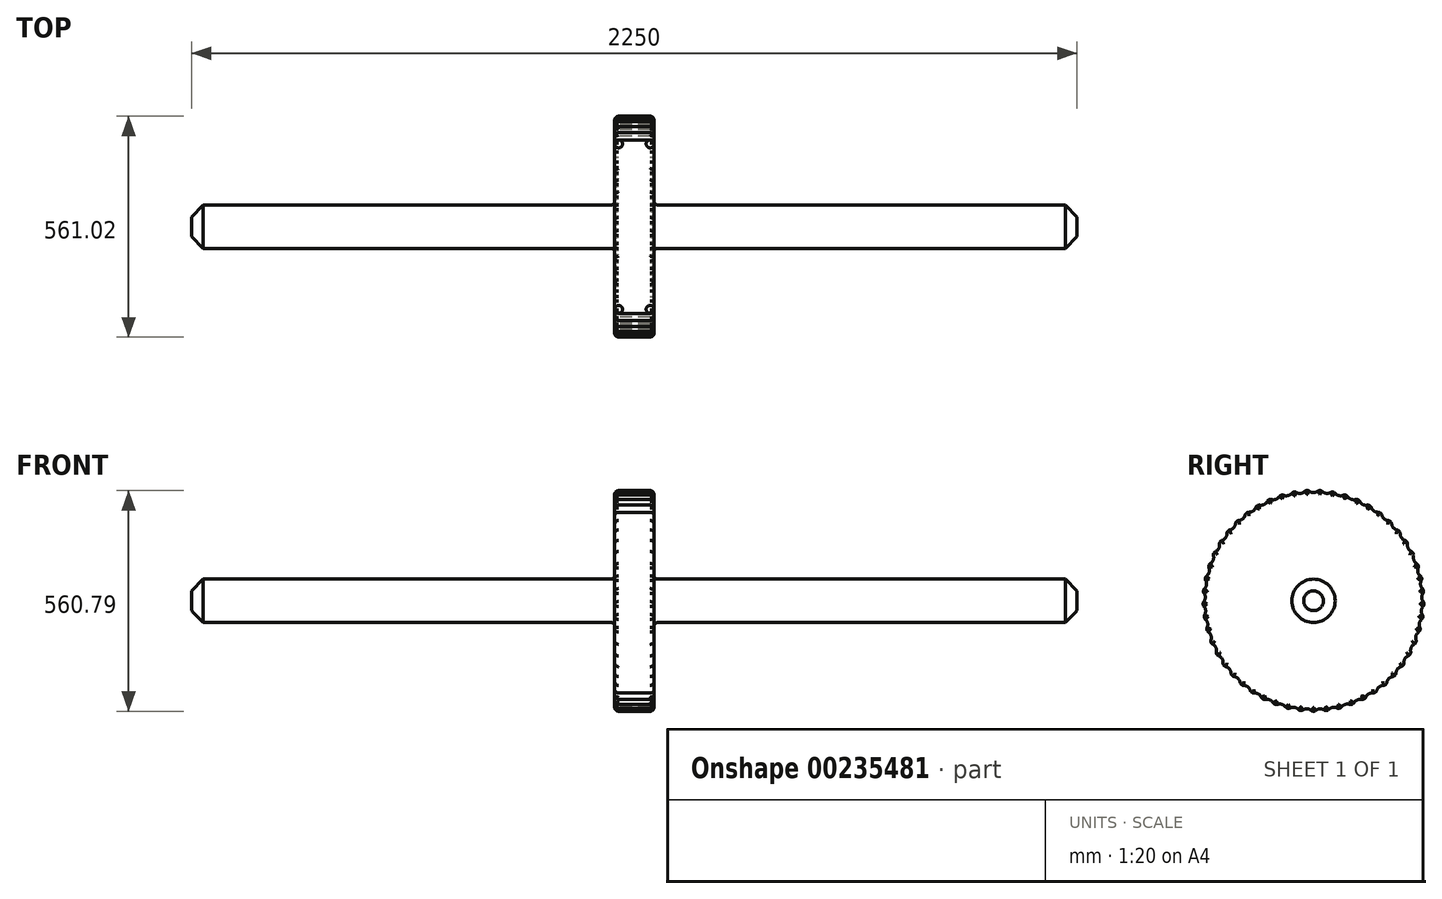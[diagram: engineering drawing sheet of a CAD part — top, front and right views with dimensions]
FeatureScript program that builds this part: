
annotation { "Feature Type Name" : "Feature", "Feature Type Description" : "" }
export const myFeature = defineFeature(function(context is Context, id is Id, definition is map)
    precondition{}
    {
        {
            var Q0;
            Q0=qCreatedBy(makeId("Right.planeOp"),FACE);
            var sketch = newSketch(context, id + "F0", { "sketchPlane" : qUnion([Q0])});
            skCircle(sketch, "E0", {"center": v(0, 0) * mm, "radius": 55 * mm});
            skSolve(sketch);
        }
        {
            var Q0;
            Q0 = qSketchRegion(id + "F0", true);
            extrude(context, id + "F1", {"entities" : qUnion([Q0]), "endBound" : BoundingType.SYMMETRIC, "depth" : 2250 * mm});
        }
        {
            var Q0;
            Q0=makeQuery(id+"F1.opExtrude","CAP_EDGE",EDGE,{"disambiguationData":[OSD([sQuery(id+"F0.wireOp",EDGE,"E0")])],"isStart":false});
            var Q1;
            Q1=makeQuery(id+"F1.opExtrude","CAP_EDGE",EDGE,{"disambiguationData":[OSD([sQuery(id+"F0.wireOp",EDGE,"E0")])],"isStart":true});
            chamfer(context, id + "F2", {"entities" : qUnion([Q0, Q1]), "width" : 30 * mm, "tangentPropagation" : true});
        }
        {
            var Q0;
            Q0=qCreatedBy(makeId("Right.planeOp"),FACE);
            var sketch = newSketch(context, id + "F3", { "sketchPlane" : qUnion([Q0])});
            skCircle(sketch, "E1", {"center": v(0, 0) * mm, "radius": 275 * mm, "construction": true});
            skCircle(sketch, "E2", {"center": v(0, 0) * mm, "radius": 310 * mm, "construction": true});
            skArc(sketch, "E3", {"start": v(-17.5, 291.98) * mm, "mid": v(0, 275) * mm, "end": v(17.5, 291.98) * mm});
            skCircle(sketch, "E4", {"center": v(0, 0) * mm, "radius": 292.5 * mm, "construction": true});
            skArc(sketch, "E5.1.0", {"start": v(-51.9, 287.86) * mm, "mid": v(-32.53, 273.07) * mm, "end": v(-17.16, 292) * mm});
            skArc(sketch, "E5.2.0", {"start": v(-85.58, 279.7) * mm, "mid": v(-64.6, 267.3) * mm, "end": v(-51.58, 287.92) * mm});
            skArc(sketch, "E5.3.0", {"start": v(-118.06, 267.61) * mm, "mid": v(-95.76, 257.8) * mm, "end": v(-85.27, 279.8) * mm});
            skArc(sketch, "E5.4.0", {"start": v(-148.89, 251.77) * mm, "mid": v(-125.57, 244.66) * mm, "end": v(-117.76, 267.75) * mm});
            skArc(sketch, "E5.5.0", {"start": v(-177.62, 232.4) * mm, "mid": v(-153.63, 228.09) * mm, "end": v(-148.6, 251.94) * mm});
            skArc(sketch, "E5.6.0", {"start": v(-203.86, 209.76) * mm, "mid": v(-179.53, 208.32) * mm, "end": v(-177.36, 232.6) * mm});
            skArc(sketch, "E5.7.0", {"start": v(-227.24, 184.17) * mm, "mid": v(-202.9, 185.62) * mm, "end": v(-203.62, 209.99) * mm});
            skArc(sketch, "E5.8.0", {"start": v(-247.42, 156) * mm, "mid": v(-223.43, 160.32) * mm, "end": v(-227.03, 184.43) * mm});
            skArc(sketch, "E5.9.0", {"start": v(-264.14, 125.65) * mm, "mid": v(-240.83, 132.77) * mm, "end": v(-247.25, 156.28) * mm});
            skArc(sketch, "E5.10.0", {"start": v(-277.15, 93.52) * mm, "mid": v(-254.84, 103.35) * mm, "end": v(-264, 125.94) * mm});
            skArc(sketch, "E5.11.0", {"start": v(-286.26, 60.09) * mm, "mid": v(-265.27, 72.49) * mm, "end": v(-277.04, 93.83) * mm});
            skArc(sketch, "E5.12.0", {"start": v(-291.36, 25.8) * mm, "mid": v(-271.99, 40.6) * mm, "end": v(-286.2, 60.4) * mm});
            skArc(sketch, "E5.13.0", {"start": v(-292.37, -8.83) * mm, "mid": v(-274.88, 8.15) * mm, "end": v(-291.33, 26.14) * mm});
            skArc(sketch, "E5.14.0", {"start": v(-289.27, -43.35) * mm, "mid": v(-273.91, -24.42) * mm, "end": v(-292.38, -8.5) * mm});
            skArc(sketch, "E5.15.0", {"start": v(-282.11, -77.26) * mm, "mid": v(-269.1, -56.64) * mm, "end": v(-289.32, -43.02) * mm});
            skArc(sketch, "E5.16.0", {"start": v(-271, -110.08) * mm, "mid": v(-260.51, -88.07) * mm, "end": v(-282.2, -76.94) * mm});
            skArc(sketch, "E5.17.0", {"start": v(-256.07, -141.36) * mm, "mid": v(-248.27, -118.27) * mm, "end": v(-271.12, -109.78) * mm});
            skArc(sketch, "E5.18.0", {"start": v(-237.56, -170.66) * mm, "mid": v(-232.54, -146.8) * mm, "end": v(-256.23, -141.07) * mm});
            skArc(sketch, "E5.19.0", {"start": v(-215.7, -197.55) * mm, "mid": v(-213.54, -173.27) * mm, "end": v(-237.75, -170.39) * mm});
            skArc(sketch, "E5.20.0", {"start": v(-190.83, -221.68) * mm, "mid": v(-191.55, -197.31) * mm, "end": v(-215.93, -197.31) * mm});
            skArc(sketch, "E5.21.0", {"start": v(-163.27, -242.7) * mm, "mid": v(-166.87, -218.58) * mm, "end": v(-191.08, -221.46) * mm});
            skArc(sketch, "E5.22.0", {"start": v(-133.42, -260.3) * mm, "mid": v(-139.85, -236.79) * mm, "end": v(-163.54, -242.5) * mm});
            skArc(sketch, "E5.23.0", {"start": v(-101.7, -274.25) * mm, "mid": v(-110.86, -251.67) * mm, "end": v(-133.71, -260.15) * mm});
            skArc(sketch, "E5.24.0", {"start": v(-68.54, -284.36) * mm, "mid": v(-80.32, -263.01) * mm, "end": v(-102, -274.14) * mm});
            skArc(sketch, "E5.25.0", {"start": v(-34.43, -290.47) * mm, "mid": v(-48.64, -270.66) * mm, "end": v(-68.86, -284.28) * mm});
            skArc(sketch, "E5.26.0", {"start": v(0.16, -292.5) * mm, "mid": v(-16.3, -274.52) * mm, "end": v(-34.76, -290.43) * mm});
            skArc(sketch, "E5.27.0", {"start": v(34.76, -290.43) * mm, "mid": v(16.3, -274.52) * mm, "end": v(-0.16, -292.5) * mm});
            skArc(sketch, "E5.28.0", {"start": v(68.86, -284.28) * mm, "mid": v(48.64, -270.66) * mm, "end": v(34.43, -290.47) * mm});
            skArc(sketch, "E5.29.0", {"start": v(102, -274.14) * mm, "mid": v(80.32, -263.01) * mm, "end": v(68.54, -284.36) * mm});
            skArc(sketch, "E5.30.0", {"start": v(133.71, -260.15) * mm, "mid": v(110.86, -251.67) * mm, "end": v(101.7, -274.25) * mm});
            skArc(sketch, "E5.31.0", {"start": v(163.54, -242.5) * mm, "mid": v(139.85, -236.79) * mm, "end": v(133.42, -260.3) * mm});
            skArc(sketch, "E5.32.0", {"start": v(191.08, -221.46) * mm, "mid": v(166.87, -218.58) * mm, "end": v(163.27, -242.7) * mm});
            skArc(sketch, "E5.33.0", {"start": v(215.93, -197.31) * mm, "mid": v(191.55, -197.31) * mm, "end": v(190.83, -221.68) * mm});
            skArc(sketch, "E5.34.0", {"start": v(237.75, -170.39) * mm, "mid": v(213.54, -173.27) * mm, "end": v(215.7, -197.55) * mm});
            skArc(sketch, "E5.35.0", {"start": v(256.23, -141.07) * mm, "mid": v(232.54, -146.8) * mm, "end": v(237.56, -170.66) * mm});
            skArc(sketch, "E5.36.0", {"start": v(271.12, -109.78) * mm, "mid": v(248.27, -118.27) * mm, "end": v(256.07, -141.36) * mm});
            skArc(sketch, "E5.37.0", {"start": v(282.2, -76.94) * mm, "mid": v(260.51, -88.07) * mm, "end": v(271, -110.08) * mm});
            skArc(sketch, "E5.38.0", {"start": v(289.32, -43.02) * mm, "mid": v(269.1, -56.64) * mm, "end": v(282.11, -77.26) * mm});
            skArc(sketch, "E5.39.0", {"start": v(292.38, -8.5) * mm, "mid": v(273.91, -24.42) * mm, "end": v(289.27, -43.35) * mm});
            skArc(sketch, "E5.40.0", {"start": v(291.33, 26.14) * mm, "mid": v(274.88, 8.15) * mm, "end": v(292.37, -8.83) * mm});
            skArc(sketch, "E5.41.0", {"start": v(286.2, 60.4) * mm, "mid": v(271.99, 40.6) * mm, "end": v(291.36, 25.8) * mm});
            skArc(sketch, "E5.42.0", {"start": v(277.04, 93.83) * mm, "mid": v(265.27, 72.49) * mm, "end": v(286.26, 60.09) * mm});
            skArc(sketch, "E5.43.0", {"start": v(264, 125.94) * mm, "mid": v(254.84, 103.35) * mm, "end": v(277.15, 93.52) * mm});
            skArc(sketch, "E5.44.0", {"start": v(247.25, 156.28) * mm, "mid": v(240.83, 132.77) * mm, "end": v(264.14, 125.65) * mm});
            skArc(sketch, "E5.45.0", {"start": v(227.03, 184.43) * mm, "mid": v(223.43, 160.32) * mm, "end": v(247.42, 156) * mm});
            skArc(sketch, "E5.46.0", {"start": v(203.62, 209.99) * mm, "mid": v(202.9, 185.62) * mm, "end": v(227.24, 184.17) * mm});
            skArc(sketch, "E5.47.0", {"start": v(177.36, 232.6) * mm, "mid": v(179.53, 208.32) * mm, "end": v(203.86, 209.76) * mm});
            skArc(sketch, "E5.48.0", {"start": v(148.6, 251.94) * mm, "mid": v(153.63, 228.09) * mm, "end": v(177.62, 232.4) * mm});
            skArc(sketch, "E5.49.0", {"start": v(117.76, 267.75) * mm, "mid": v(125.57, 244.66) * mm, "end": v(148.89, 251.77) * mm});
            skArc(sketch, "E6.2.50.0", {"start": v(85.27, 279.8) * mm, "mid": v(95.76, 257.8) * mm, "end": v(118.06, 267.61) * mm});
            skArc(sketch, "E6.2.51.0", {"start": v(51.58, 287.92) * mm, "mid": v(64.6, 267.3) * mm, "end": v(85.58, 279.7) * mm});
            skArc(sketch, "E7.2.52.0", {"start": v(17.16, 292) * mm, "mid": v(32.53, 273.07) * mm, "end": v(51.9, 287.86) * mm});
            skSolve(sketch);
        }
        {
            var Q0;
            Q0=makeQuery(id+"F3.imprint","IMPRINT",FACE,{"disambiguationData":[TD([[makeQuery(id+"F3.imprint","IMPRINT",EDGE,{"derivedFrom":sQuery(id+"F3.wireOp",EDGE,"E1")}),1.0]])]});
            var Q1;
            {var subQ48=sQuery(id+"F3.wireOp",EDGE,"E5.1.0");var subQ49=sQuery(id+"F3.wireOp",EDGE,"E3");var subQ50=makeQuery(id+"F3.imprint","INTERSECT",VERTEX,{"derivedFrom":[subQ49,subQ48]});Q1=makeQuery(id+"F3.imprint","IMPRINT",FACE,{"disambiguationData":[TD([[makeQuery(id+"F3.imprint","IMPRINT",EDGE,{"disambiguationData":[TD([[subQ50,-1.0]])],"derivedFrom":subQ49}),-1.0]])]});}
            extrude(context, id + "F4", {"entities" : qUnion([Q0, Q1]), "operationType" : NewBodyOperationType.ADD, "endBound" : BoundingType.SYMMETRIC, "depth" : 100 * mm});
        }
        {
            var Q0;
            Q0=makeQuery(id+"F4.opExtrude","CAP_FACE",FACE,{"disambiguationData":[OSD([sQuery(id+"F3.wireOp",EDGE,"E3"),sQuery(id+"F3.wireOp",EDGE,"E5.1.0"),sQuery(id+"F3.wireOp",EDGE,"E5.2.0"),sQuery(id+"F3.wireOp",EDGE,"E5.3.0"),sQuery(id+"F3.wireOp",EDGE,"E5.4.0"),sQuery(id+"F3.wireOp",EDGE,"E5.5.0"),sQuery(id+"F3.wireOp",EDGE,"E5.6.0"),sQuery(id+"F3.wireOp",EDGE,"E5.7.0"),sQuery(id+"F3.wireOp",EDGE,"E5.8.0"),sQuery(id+"F3.wireOp",EDGE,"E5.9.0"),sQuery(id+"F3.wireOp",EDGE,"E5.10.0"),sQuery(id+"F3.wireOp",EDGE,"E5.11.0"),sQuery(id+"F3.wireOp",EDGE,"E5.12.0"),sQuery(id+"F3.wireOp",EDGE,"E5.13.0"),sQuery(id+"F3.wireOp",EDGE,"E5.14.0"),sQuery(id+"F3.wireOp",EDGE,"E5.15.0"),sQuery(id+"F3.wireOp",EDGE,"E5.16.0"),sQuery(id+"F3.wireOp",EDGE,"E5.17.0"),sQuery(id+"F3.wireOp",EDGE,"E5.18.0"),sQuery(id+"F3.wireOp",EDGE,"E5.19.0"),sQuery(id+"F3.wireOp",EDGE,"E5.20.0"),sQuery(id+"F3.wireOp",EDGE,"E5.21.0"),sQuery(id+"F3.wireOp",EDGE,"E5.22.0"),sQuery(id+"F3.wireOp",EDGE,"E5.23.0"),sQuery(id+"F3.wireOp",EDGE,"E5.24.0"),sQuery(id+"F3.wireOp",EDGE,"E5.25.0"),sQuery(id+"F3.wireOp",EDGE,"E5.26.0"),sQuery(id+"F3.wireOp",EDGE,"E5.27.0"),sQuery(id+"F3.wireOp",EDGE,"E5.28.0"),sQuery(id+"F3.wireOp",EDGE,"E5.29.0"),sQuery(id+"F3.wireOp",EDGE,"E5.30.0"),sQuery(id+"F3.wireOp",EDGE,"E5.31.0"),sQuery(id+"F3.wireOp",EDGE,"E5.32.0"),sQuery(id+"F3.wireOp",EDGE,"E5.33.0"),sQuery(id+"F3.wireOp",EDGE,"E5.34.0"),sQuery(id+"F3.wireOp",EDGE,"E5.35.0"),sQuery(id+"F3.wireOp",EDGE,"E5.36.0"),sQuery(id+"F3.wireOp",EDGE,"E5.37.0"),sQuery(id+"F3.wireOp",EDGE,"E5.38.0"),sQuery(id+"F3.wireOp",EDGE,"E5.39.0"),sQuery(id+"F3.wireOp",EDGE,"E5.40.0"),sQuery(id+"F3.wireOp",EDGE,"E5.41.0"),sQuery(id+"F3.wireOp",EDGE,"E5.42.0"),sQuery(id+"F3.wireOp",EDGE,"E5.43.0"),sQuery(id+"F3.wireOp",EDGE,"E5.44.0"),sQuery(id+"F3.wireOp",EDGE,"E5.45.0"),sQuery(id+"F3.wireOp",EDGE,"E5.46.0"),sQuery(id+"F3.wireOp",EDGE,"E5.47.0"),sQuery(id+"F3.wireOp",EDGE,"E5.48.0"),sQuery(id+"F3.wireOp",EDGE,"E5.49.0"),sQuery(id+"F3.wireOp",EDGE,"E6.2.50.0"),sQuery(id+"F3.wireOp",EDGE,"E6.2.51.0"),sQuery(id+"F3.wireOp",EDGE,"E7.2.52.0")])],"isStart":false});
            var Q1;
            Q1=makeQuery(id+"F4.opExtrude","CAP_FACE",FACE,{"disambiguationData":[OSD([sQuery(id+"F3.wireOp",EDGE,"E3"),sQuery(id+"F3.wireOp",EDGE,"E5.1.0"),sQuery(id+"F3.wireOp",EDGE,"E5.2.0"),sQuery(id+"F3.wireOp",EDGE,"E5.3.0"),sQuery(id+"F3.wireOp",EDGE,"E5.4.0"),sQuery(id+"F3.wireOp",EDGE,"E5.5.0"),sQuery(id+"F3.wireOp",EDGE,"E5.6.0"),sQuery(id+"F3.wireOp",EDGE,"E5.7.0"),sQuery(id+"F3.wireOp",EDGE,"E5.8.0"),sQuery(id+"F3.wireOp",EDGE,"E5.9.0"),sQuery(id+"F3.wireOp",EDGE,"E5.10.0"),sQuery(id+"F3.wireOp",EDGE,"E5.11.0"),sQuery(id+"F3.wireOp",EDGE,"E5.12.0"),sQuery(id+"F3.wireOp",EDGE,"E5.13.0"),sQuery(id+"F3.wireOp",EDGE,"E5.14.0"),sQuery(id+"F3.wireOp",EDGE,"E5.15.0"),sQuery(id+"F3.wireOp",EDGE,"E5.16.0"),sQuery(id+"F3.wireOp",EDGE,"E5.17.0"),sQuery(id+"F3.wireOp",EDGE,"E5.18.0"),sQuery(id+"F3.wireOp",EDGE,"E5.19.0"),sQuery(id+"F3.wireOp",EDGE,"E5.20.0"),sQuery(id+"F3.wireOp",EDGE,"E5.21.0"),sQuery(id+"F3.wireOp",EDGE,"E5.22.0"),sQuery(id+"F3.wireOp",EDGE,"E5.23.0"),sQuery(id+"F3.wireOp",EDGE,"E5.24.0"),sQuery(id+"F3.wireOp",EDGE,"E5.25.0"),sQuery(id+"F3.wireOp",EDGE,"E5.26.0"),sQuery(id+"F3.wireOp",EDGE,"E5.27.0"),sQuery(id+"F3.wireOp",EDGE,"E5.28.0"),sQuery(id+"F3.wireOp",EDGE,"E5.29.0"),sQuery(id+"F3.wireOp",EDGE,"E5.30.0"),sQuery(id+"F3.wireOp",EDGE,"E5.31.0"),sQuery(id+"F3.wireOp",EDGE,"E5.32.0"),sQuery(id+"F3.wireOp",EDGE,"E5.33.0"),sQuery(id+"F3.wireOp",EDGE,"E5.34.0"),sQuery(id+"F3.wireOp",EDGE,"E5.35.0"),sQuery(id+"F3.wireOp",EDGE,"E5.36.0"),sQuery(id+"F3.wireOp",EDGE,"E5.37.0"),sQuery(id+"F3.wireOp",EDGE,"E5.38.0"),sQuery(id+"F3.wireOp",EDGE,"E5.39.0"),sQuery(id+"F3.wireOp",EDGE,"E5.40.0"),sQuery(id+"F3.wireOp",EDGE,"E5.41.0"),sQuery(id+"F3.wireOp",EDGE,"E5.42.0"),sQuery(id+"F3.wireOp",EDGE,"E5.43.0"),sQuery(id+"F3.wireOp",EDGE,"E5.44.0"),sQuery(id+"F3.wireOp",EDGE,"E5.45.0"),sQuery(id+"F3.wireOp",EDGE,"E5.46.0"),sQuery(id+"F3.wireOp",EDGE,"E5.47.0"),sQuery(id+"F3.wireOp",EDGE,"E5.48.0"),sQuery(id+"F3.wireOp",EDGE,"E5.49.0"),sQuery(id+"F3.wireOp",EDGE,"E6.2.50.0"),sQuery(id+"F3.wireOp",EDGE,"E6.2.51.0"),sQuery(id+"F3.wireOp",EDGE,"E7.2.52.0")])],"isStart":true});
            fillet(context, id + "F5", {"entities" : qUnion([Q0, Q1]), "radius" : 10 * mm, "tangentPropagation" : true, "allowEdgeOverflow" : false});
        }
        {
            var Q0;
            Q0=makeQuery(id+"F4.opExtrude","SWEPT_EDGE",EDGE,{"disambiguationData":[OSD([sQuery(id+"F3.wireOp",EDGE,"E5.22.0"),sQuery(id+"F3.wireOp",EDGE,"E5.23.0")])]});
            var Q1;
            Q1=makeQuery(id+"F4.opExtrude","SWEPT_EDGE",EDGE,{"disambiguationData":[OSD([sQuery(id+"F3.wireOp",EDGE,"E5.21.0"),sQuery(id+"F3.wireOp",EDGE,"E5.22.0")])]});
            var Q2;
            Q2=makeQuery(id+"F4.opExtrude","SWEPT_EDGE",EDGE,{"disambiguationData":[OSD([sQuery(id+"F3.wireOp",EDGE,"E5.20.0"),sQuery(id+"F3.wireOp",EDGE,"E5.21.0")])]});
            var Q3;
            Q3=makeQuery(id+"F4.opExtrude","SWEPT_EDGE",EDGE,{"disambiguationData":[OSD([sQuery(id+"F3.wireOp",EDGE,"E5.18.0"),sQuery(id+"F3.wireOp",EDGE,"E5.19.0")])]});
            var Q4;
            Q4=makeQuery(id+"F4.opExtrude","SWEPT_EDGE",EDGE,{"disambiguationData":[OSD([sQuery(id+"F3.wireOp",EDGE,"E5.17.0"),sQuery(id+"F3.wireOp",EDGE,"E5.18.0")])]});
            var Q5;
            Q5=makeQuery(id+"F4.opExtrude","SWEPT_EDGE",EDGE,{"disambiguationData":[OSD([sQuery(id+"F3.wireOp",EDGE,"E5.19.0"),sQuery(id+"F3.wireOp",EDGE,"E5.20.0")])]});
            var Q6;
            Q6=makeQuery(id+"F4.opExtrude","SWEPT_EDGE",EDGE,{"disambiguationData":[OSD([sQuery(id+"F3.wireOp",EDGE,"E5.16.0"),sQuery(id+"F3.wireOp",EDGE,"E5.17.0")])]});
            var Q7;
            Q7=makeQuery(id+"F4.opExtrude","SWEPT_EDGE",EDGE,{"disambiguationData":[OSD([sQuery(id+"F3.wireOp",EDGE,"E5.15.0"),sQuery(id+"F3.wireOp",EDGE,"E5.16.0")])]});
            var Q8;
            Q8=makeQuery(id+"F4.opExtrude","SWEPT_EDGE",EDGE,{"disambiguationData":[OSD([sQuery(id+"F3.wireOp",EDGE,"E5.14.0"),sQuery(id+"F3.wireOp",EDGE,"E5.15.0")])]});
            var Q9;
            Q9=makeQuery(id+"F4.opExtrude","SWEPT_EDGE",EDGE,{"disambiguationData":[OSD([sQuery(id+"F3.wireOp",EDGE,"E5.13.0"),sQuery(id+"F3.wireOp",EDGE,"E5.14.0")])]});
            var Q10;
            Q10=makeQuery(id+"F4.opExtrude","SWEPT_EDGE",EDGE,{"disambiguationData":[OSD([sQuery(id+"F3.wireOp",EDGE,"E5.12.0"),sQuery(id+"F3.wireOp",EDGE,"E5.13.0")])]});
            var Q11;
            Q11=makeQuery(id+"F4.opExtrude","SWEPT_EDGE",EDGE,{"disambiguationData":[OSD([sQuery(id+"F3.wireOp",EDGE,"E5.11.0"),sQuery(id+"F3.wireOp",EDGE,"E5.12.0")])]});
            var Q12;
            Q12=makeQuery(id+"F4.opExtrude","SWEPT_EDGE",EDGE,{"disambiguationData":[OSD([sQuery(id+"F3.wireOp",EDGE,"E5.10.0"),sQuery(id+"F3.wireOp",EDGE,"E5.11.0")])]});
            var Q13;
            Q13=makeQuery(id+"F4.opExtrude","SWEPT_EDGE",EDGE,{"disambiguationData":[OSD([sQuery(id+"F3.wireOp",EDGE,"E5.9.0"),sQuery(id+"F3.wireOp",EDGE,"E5.10.0")])]});
            var Q14;
            Q14=makeQuery(id+"F4.opExtrude","SWEPT_EDGE",EDGE,{"disambiguationData":[OSD([sQuery(id+"F3.wireOp",EDGE,"E5.8.0"),sQuery(id+"F3.wireOp",EDGE,"E5.9.0")])]});
            var Q15;
            Q15=makeQuery(id+"F4.opExtrude","SWEPT_EDGE",EDGE,{"disambiguationData":[OSD([sQuery(id+"F3.wireOp",EDGE,"E5.7.0"),sQuery(id+"F3.wireOp",EDGE,"E5.8.0")])]});
            var Q16;
            Q16=makeQuery(id+"F4.opExtrude","SWEPT_EDGE",EDGE,{"disambiguationData":[OSD([sQuery(id+"F3.wireOp",EDGE,"E5.8.0"),sQuery(id+"F3.wireOp",EDGE,"E5.9.0")])]});
            var Q17;
            Q17=makeQuery(id+"F4.opExtrude","SWEPT_EDGE",EDGE,{"disambiguationData":[OSD([sQuery(id+"F3.wireOp",EDGE,"E5.6.0"),sQuery(id+"F3.wireOp",EDGE,"E5.7.0")])]});
            var Q18;
            Q18=makeQuery(id+"F4.opExtrude","SWEPT_EDGE",EDGE,{"disambiguationData":[OSD([sQuery(id+"F3.wireOp",EDGE,"E5.5.0"),sQuery(id+"F3.wireOp",EDGE,"E5.6.0")])]});
            var Q19;
            Q19=makeQuery(id+"F4.opExtrude","SWEPT_EDGE",EDGE,{"disambiguationData":[OSD([sQuery(id+"F3.wireOp",EDGE,"E5.4.0"),sQuery(id+"F3.wireOp",EDGE,"E5.5.0")])]});
            var Q20;
            Q20=makeQuery(id+"F4.opExtrude","SWEPT_EDGE",EDGE,{"disambiguationData":[OSD([sQuery(id+"F3.wireOp",EDGE,"E5.3.0"),sQuery(id+"F3.wireOp",EDGE,"E5.4.0")])]});
            var Q21;
            Q21=makeQuery(id+"F4.opExtrude","SWEPT_EDGE",EDGE,{"disambiguationData":[OSD([sQuery(id+"F3.wireOp",EDGE,"E5.2.0"),sQuery(id+"F3.wireOp",EDGE,"E5.3.0")])]});
            var Q22;
            Q22=makeQuery(id+"F4.opExtrude","SWEPT_EDGE",EDGE,{"disambiguationData":[OSD([sQuery(id+"F3.wireOp",EDGE,"E5.1.0"),sQuery(id+"F3.wireOp",EDGE,"E5.2.0")])]});
            var Q23;
            Q23=makeQuery(id+"F4.opExtrude","SWEPT_EDGE",EDGE,{"disambiguationData":[OSD([sQuery(id+"F3.wireOp",EDGE,"E3"),sQuery(id+"F3.wireOp",EDGE,"E5.1.0")])]});
            var Q24;
            Q24=makeQuery(id+"F4.opExtrude","SWEPT_EDGE",EDGE,{"disambiguationData":[OSD([sQuery(id+"F3.wireOp",EDGE,"E3"),sQuery(id+"F3.wireOp",EDGE,"E7.2.52.0")])]});
            var Q25;
            Q25=makeQuery(id+"F4.opExtrude","SWEPT_EDGE",EDGE,{"disambiguationData":[OSD([sQuery(id+"F3.wireOp",EDGE,"E6.2.51.0"),sQuery(id+"F3.wireOp",EDGE,"E7.2.52.0")])]});
            var Q26;
            Q26=makeQuery(id+"F4.opExtrude","SWEPT_EDGE",EDGE,{"disambiguationData":[OSD([sQuery(id+"F3.wireOp",EDGE,"E6.2.50.0"),sQuery(id+"F3.wireOp",EDGE,"E6.2.51.0")])]});
            var Q27;
            Q27=makeQuery(id+"F4.opExtrude","SWEPT_EDGE",EDGE,{"disambiguationData":[OSD([sQuery(id+"F3.wireOp",EDGE,"E5.49.0"),sQuery(id+"F3.wireOp",EDGE,"E6.2.50.0")])]});
            var Q28;
            Q28=makeQuery(id+"F4.opExtrude","SWEPT_EDGE",EDGE,{"disambiguationData":[OSD([sQuery(id+"F3.wireOp",EDGE,"E5.48.0"),sQuery(id+"F3.wireOp",EDGE,"E5.49.0")])]});
            var Q29;
            Q29=makeQuery(id+"F4.opExtrude","SWEPT_EDGE",EDGE,{"disambiguationData":[OSD([sQuery(id+"F3.wireOp",EDGE,"E5.47.0"),sQuery(id+"F3.wireOp",EDGE,"E5.48.0")])]});
            var Q30;
            Q30=makeQuery(id+"F4.opExtrude","SWEPT_EDGE",EDGE,{"disambiguationData":[OSD([sQuery(id+"F3.wireOp",EDGE,"E5.46.0"),sQuery(id+"F3.wireOp",EDGE,"E5.47.0")])]});
            var Q31;
            Q31=makeQuery(id+"F4.opExtrude","SWEPT_EDGE",EDGE,{"disambiguationData":[OSD([sQuery(id+"F3.wireOp",EDGE,"E5.45.0"),sQuery(id+"F3.wireOp",EDGE,"E5.46.0")])]});
            var Q32;
            Q32=makeQuery(id+"F4.opExtrude","SWEPT_EDGE",EDGE,{"disambiguationData":[OSD([sQuery(id+"F3.wireOp",EDGE,"E5.44.0"),sQuery(id+"F3.wireOp",EDGE,"E5.45.0")])]});
            var Q33;
            Q33=makeQuery(id+"F4.opExtrude","SWEPT_EDGE",EDGE,{"disambiguationData":[OSD([sQuery(id+"F3.wireOp",EDGE,"E5.43.0"),sQuery(id+"F3.wireOp",EDGE,"E5.44.0")])]});
            var Q34;
            Q34=makeQuery(id+"F4.opExtrude","SWEPT_EDGE",EDGE,{"disambiguationData":[OSD([sQuery(id+"F3.wireOp",EDGE,"E5.42.0"),sQuery(id+"F3.wireOp",EDGE,"E5.43.0")])]});
            var Q35;
            Q35=makeQuery(id+"F4.opExtrude","SWEPT_EDGE",EDGE,{"disambiguationData":[OSD([sQuery(id+"F3.wireOp",EDGE,"E5.41.0"),sQuery(id+"F3.wireOp",EDGE,"E5.42.0")])]});
            var Q36;
            Q36=makeQuery(id+"F4.opExtrude","SWEPT_EDGE",EDGE,{"disambiguationData":[OSD([sQuery(id+"F3.wireOp",EDGE,"E5.40.0"),sQuery(id+"F3.wireOp",EDGE,"E5.41.0")])]});
            var Q37;
            Q37=makeQuery(id+"F4.opExtrude","SWEPT_EDGE",EDGE,{"disambiguationData":[OSD([sQuery(id+"F3.wireOp",EDGE,"E5.39.0"),sQuery(id+"F3.wireOp",EDGE,"E5.40.0")])]});
            var Q38;
            Q38=makeQuery(id+"F4.opExtrude","SWEPT_EDGE",EDGE,{"disambiguationData":[OSD([sQuery(id+"F3.wireOp",EDGE,"E5.38.0"),sQuery(id+"F3.wireOp",EDGE,"E5.39.0")])]});
            var Q39;
            Q39=makeQuery(id+"F4.opExtrude","SWEPT_EDGE",EDGE,{"disambiguationData":[OSD([sQuery(id+"F3.wireOp",EDGE,"E5.37.0"),sQuery(id+"F3.wireOp",EDGE,"E5.38.0")])]});
            var Q40;
            Q40=makeQuery(id+"F4.opExtrude","SWEPT_EDGE",EDGE,{"disambiguationData":[OSD([sQuery(id+"F3.wireOp",EDGE,"E5.36.0"),sQuery(id+"F3.wireOp",EDGE,"E5.37.0")])]});
            var Q41;
            Q41=makeQuery(id+"F4.opExtrude","SWEPT_EDGE",EDGE,{"disambiguationData":[OSD([sQuery(id+"F3.wireOp",EDGE,"E5.35.0"),sQuery(id+"F3.wireOp",EDGE,"E5.36.0")])]});
            var Q42;
            Q42=makeQuery(id+"F4.opExtrude","SWEPT_EDGE",EDGE,{"disambiguationData":[OSD([sQuery(id+"F3.wireOp",EDGE,"E5.34.0"),sQuery(id+"F3.wireOp",EDGE,"E5.35.0")])]});
            var Q43;
            Q43=makeQuery(id+"F4.opExtrude","SWEPT_EDGE",EDGE,{"disambiguationData":[OSD([sQuery(id+"F3.wireOp",EDGE,"E5.33.0"),sQuery(id+"F3.wireOp",EDGE,"E5.34.0")])]});
            var Q44;
            Q44=makeQuery(id+"F4.opExtrude","SWEPT_EDGE",EDGE,{"disambiguationData":[OSD([sQuery(id+"F3.wireOp",EDGE,"E5.32.0"),sQuery(id+"F3.wireOp",EDGE,"E5.33.0")])]});
            var Q45;
            Q45=makeQuery(id+"F4.opExtrude","SWEPT_EDGE",EDGE,{"disambiguationData":[OSD([sQuery(id+"F3.wireOp",EDGE,"E5.31.0"),sQuery(id+"F3.wireOp",EDGE,"E5.32.0")])]});
            var Q46;
            Q46=makeQuery(id+"F4.opExtrude","SWEPT_EDGE",EDGE,{"disambiguationData":[OSD([sQuery(id+"F3.wireOp",EDGE,"E5.30.0"),sQuery(id+"F3.wireOp",EDGE,"E5.31.0")])]});
            var Q47;
            Q47=makeQuery(id+"F4.opExtrude","SWEPT_EDGE",EDGE,{"disambiguationData":[OSD([sQuery(id+"F3.wireOp",EDGE,"E5.29.0"),sQuery(id+"F3.wireOp",EDGE,"E5.30.0")])]});
            var Q48;
            Q48=makeQuery(id+"F4.opExtrude","SWEPT_EDGE",EDGE,{"disambiguationData":[OSD([sQuery(id+"F3.wireOp",EDGE,"E5.28.0"),sQuery(id+"F3.wireOp",EDGE,"E5.29.0")])]});
            var Q49;
            Q49=makeQuery(id+"F4.opExtrude","SWEPT_EDGE",EDGE,{"disambiguationData":[OSD([sQuery(id+"F3.wireOp",EDGE,"E5.27.0"),sQuery(id+"F3.wireOp",EDGE,"E5.28.0")])]});
            var Q50;
            Q50=makeQuery(id+"F4.opExtrude","SWEPT_EDGE",EDGE,{"disambiguationData":[OSD([sQuery(id+"F3.wireOp",EDGE,"E5.23.0"),sQuery(id+"F3.wireOp",EDGE,"E5.24.0")])]});
            var Q51;
            Q51=makeQuery(id+"F4.opExtrude","SWEPT_EDGE",EDGE,{"disambiguationData":[OSD([sQuery(id+"F3.wireOp",EDGE,"E5.24.0"),sQuery(id+"F3.wireOp",EDGE,"E5.25.0")])]});
            var Q52;
            Q52=makeQuery(id+"F4.opExtrude","SWEPT_EDGE",EDGE,{"disambiguationData":[OSD([sQuery(id+"F3.wireOp",EDGE,"E5.25.0"),sQuery(id+"F3.wireOp",EDGE,"E5.26.0")])]});
            var Q53;
            Q53=makeQuery(id+"F4.opExtrude","SWEPT_EDGE",EDGE,{"disambiguationData":[OSD([sQuery(id+"F3.wireOp",EDGE,"E5.26.0"),sQuery(id+"F3.wireOp",EDGE,"E5.27.0")])]});
            var Q54;
            Q54=qNothing();
            var Q55;
            Q55=qNothing();
            fillet(context, id + "F6", {"entities" : qUnion([Q0, Q1, Q2, Q3, Q4, Q5, Q6, Q7, Q8, Q9, Q10, Q11, Q12, Q13, Q14, Q15, Q16, Q17, Q18, Q19, Q20, Q21, Q22, Q23, Q24, Q25, Q26, Q27, Q28, Q29, Q30, Q31, Q32, Q33, Q34, Q35, Q36, Q37, Q38, Q39, Q40, Q41, Q42, Q43, Q44, Q45, Q46, Q47, Q48, Q49, Q50, Q51, Q52, Q53, Q54, Q55]), "radius" : 10 * mm, "tangentPropagation" : true, "allowEdgeOverflow" : false});
        }
    });
